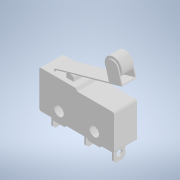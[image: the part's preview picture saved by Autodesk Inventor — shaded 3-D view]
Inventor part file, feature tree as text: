
AUTODESK INVENTOR PART (.ipt)
format: ipt  version: 2022.2 (Build 262287010, 287A)  size: 154,112 bytes
history: native  units: mm
features: mirror x1, other x1
ambient origin geometry x8: Origin, YZ Plane, XZ Plane, XY Plane, X Axis, Y Axis, Z Axis, Center Point
bodies: Volumenkörper1 (feature_tree), Volumenkörper2 (feature_tree)
feature tree (2):
  mirror  "Simetría1"
  other  "Saliente-Extruir9"
